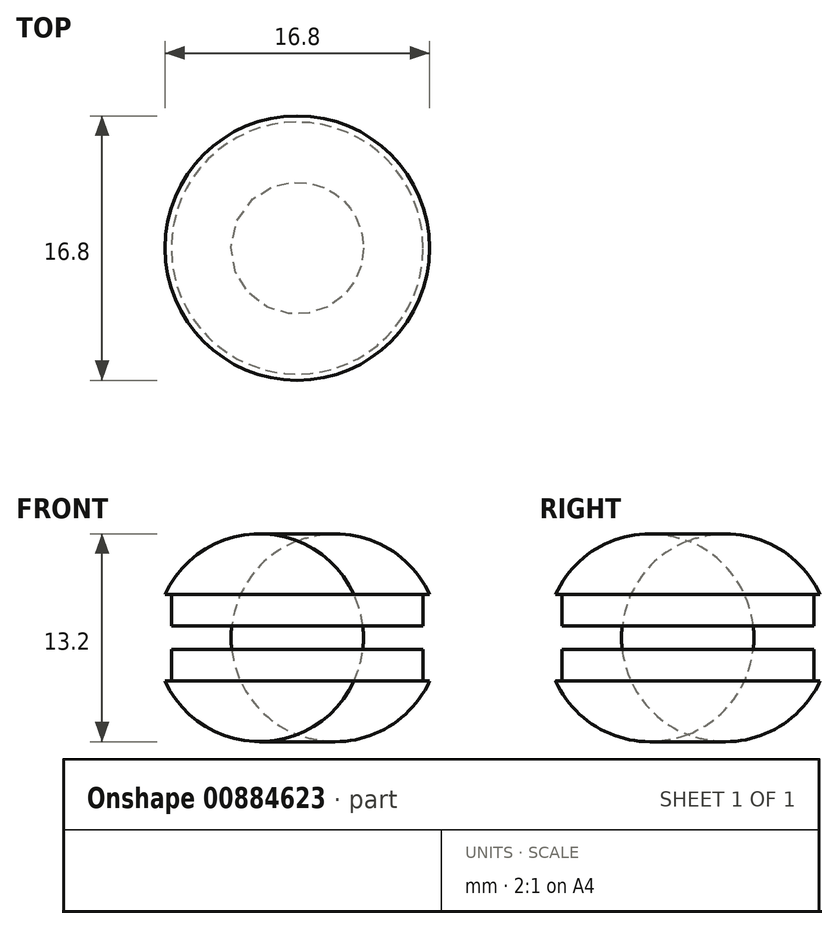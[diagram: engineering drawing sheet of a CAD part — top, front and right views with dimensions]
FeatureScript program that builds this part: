
annotation { "Feature Type Name" : "Feature", "Feature Type Description" : "" }
export const myFeature = defineFeature(function(context is Context, id is Id, definition is map)
    precondition{}
    {
        {
            var Q0;
            Q0=qCreatedBy(makeId("Front.planeOp"),FACE);
            var sketch = newSketch(context, id + "F0", { "sketchPlane" : qUnion([Q0])});
            skLineSegment(sketch, "E0", {"start": v(-42.5, 0) * mm, "end": v(78.36, 0) * mm, "construction": true});
            skLineSegment(sketch, "E1", {"start": v(0, -0.75) * mm, "end": v(0, 0) * mm});
            skLineSegment(sketch, "E2", {"start": v(0, -0.75) * mm, "end": v(8, -0.75) * mm});
            skLineSegment(sketch, "E3.MirrorCS", {"start": v(0, 0.75) * mm, "end": v(0, 0) * mm});
            skLineSegment(sketch, "E4.MirrorCS", {"start": v(0, 0.75) * mm, "end": v(8, 0.75) * mm});
            skLineSegment(sketch, "E5.MirrorCS", {"start": v(8, -0.75) * mm, "end": v(8, -2.75) * mm});
            skLineSegment(sketch, "E6", {"start": v(0, 21.33) * mm, "end": v(0, -27.49) * mm, "construction": true});
            skPoint(sketch, "E7.orphan", {"position": v(8, 0.75) * mm});
            skLineSegment(sketch, "E8.trimOffspring", {"start": v(8, 0.75) * mm, "end": v(8, 2.75) * mm});
            skLineSegment(sketch, "E9", {"start": v(8, 2.75) * mm, "end": v(8.4, 2.75) * mm});
            skLineSegment(sketch, "E10.MirrorCS", {"start": v(8, -2.75) * mm, "end": v(8.4, -2.75) * mm});
            skArc(sketch, "E11", {"start": v(8.4, -2.75) * mm, "mid": v(9, 0) * mm, "end": v(8.4, 2.75) * mm});
            skSolve(sketch);
        }
        {
            var Q0;
            Q0=makeQuery(id+"F0.imprint","IMPRINT",FACE,{"disambiguationData":[TD([[makeQuery(id+"F0.imprint","IMPRINT",EDGE,{"derivedFrom":sQuery(id+"F0.wireOp",EDGE,"E1")}),-1.0]])]});
            var Q1;
            Q1=sQuery(id+"F0.wireOp",EDGE,"E1");
            revolve(context, id + "F1", {"surfaceOperationType" : NewSurfaceOperationType.NEW, "entities" : qUnion([Q0]), "axis" : qUnion([Q1]), "revolveType" : RevolveType.FULL});
        }
    });
